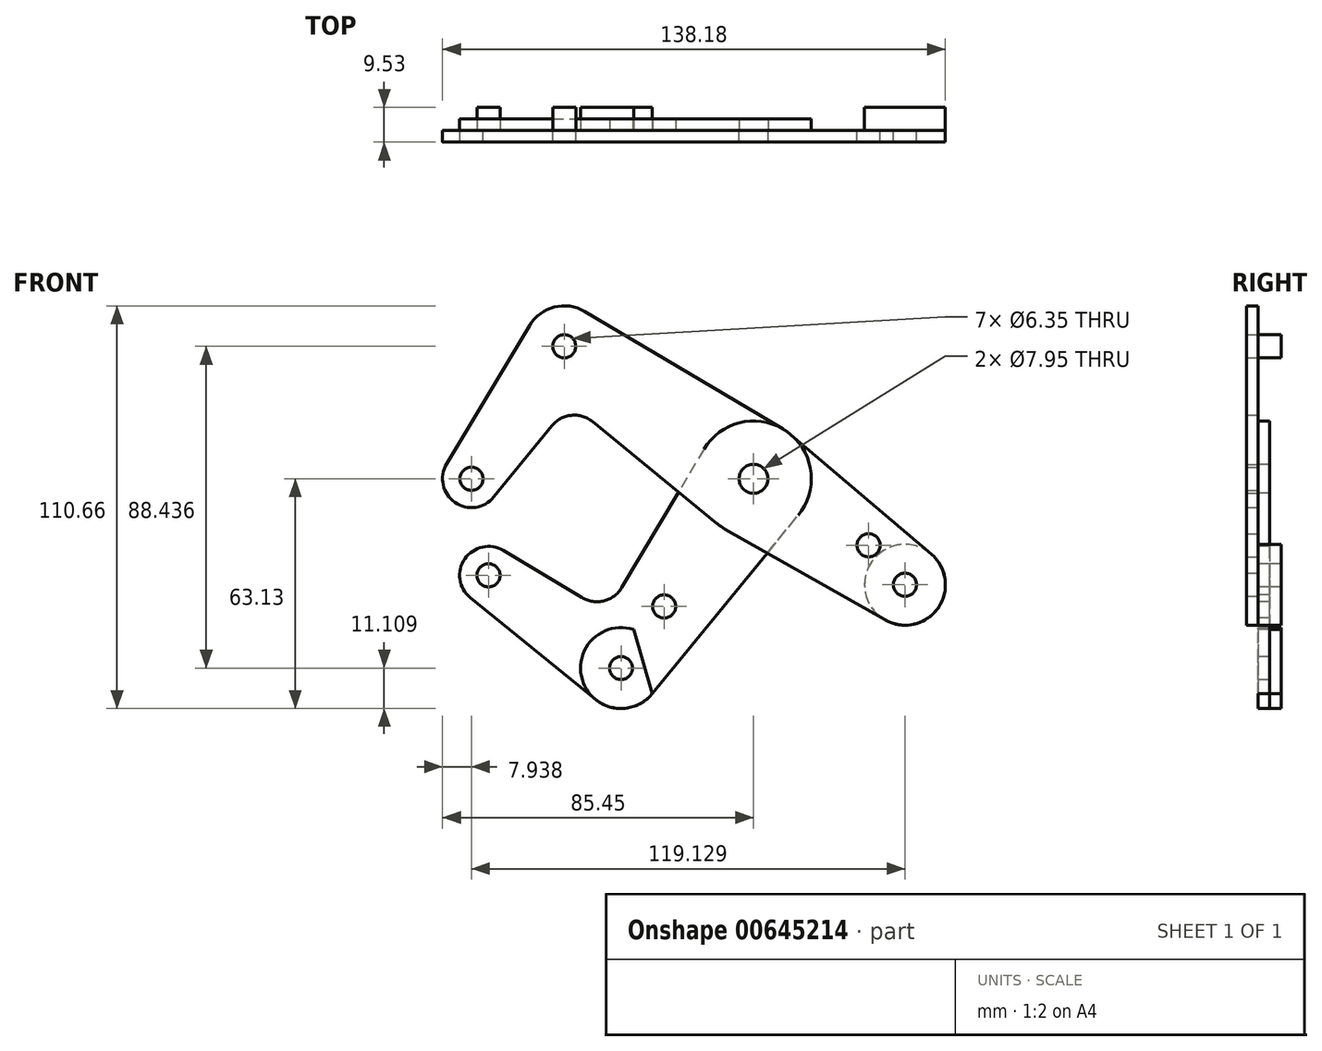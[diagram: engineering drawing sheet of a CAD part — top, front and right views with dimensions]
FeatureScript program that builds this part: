
annotation { "Feature Type Name" : "Feature", "Feature Type Description" : "" }
export const myFeature = defineFeature(function(context is Context, id is Id, definition is map)
    precondition{}
    {
        {
            var Q0;
            Q0=qCreatedBy(makeId("Front.planeOp"),FACE);
            var sketch = newSketch(context, id + "F0", { "sketchPlane" : qUnion([Q0])});
            skLineSegment(sketch, "E0", {"start": v(-77.51, 0) * mm, "end": v(-52.02, 36.41) * mm, "construction": true});
            skCircle(sketch, "E1", {"center": v(-77.51, 0) * mm, "radius": 3.18 * mm});
            skCircle(sketch, "E2", {"center": v(-77.51, 0) * mm, "radius": 7.94 * mm});
            skCircle(sketch, "E3", {"center": v(-52.02, 36.41) * mm, "radius": 3.18 * mm});
            skCircle(sketch, "E4", {"center": v(-52.02, 36.41) * mm, "radius": 11.11 * mm});
            skCircle(sketch, "E5", {"center": v(0, 0) * mm, "radius": 3.18 * mm});
            skCircle(sketch, "E6", {"center": v(0, 0) * mm, "radius": 3.98 * mm});
            skCircle(sketch, "E7", {"center": v(0, 0) * mm, "radius": 15.88 * mm});
            skCircle(sketch, "E8", {"center": v(41.62, -29.13) * mm, "radius": 3.18 * mm});
            skCircle(sketch, "E9", {"center": v(41.62, -29.13) * mm, "radius": 11.11 * mm});
            skCircle(sketch, "E10", {"center": v(31.63, -18.27) * mm, "radius": 3.18 * mm});
            skLineSegment(sketch, "E11", {"start": v(-84.32, 4.08) * mm, "end": v(-61.56, 42.12) * mm});
            skLineSegment(sketch, "E12", {"start": v(-46.35, 45.97) * mm, "end": v(8.1, 13.65) * mm});
            skLineSegment(sketch, "E13", {"start": v(10.28, 12.1) * mm, "end": v(48.81, -20.67) * mm});
            skLineSegment(sketch, "E14", {"start": v(-71.35, -5) * mm, "end": v(-55.46, 14.56) * mm});
            skLineSegment(sketch, "E15", {"start": v(-10.05, -12.29) * mm, "end": v(-44.25, 15.7) * mm});
            skLineSegment(sketch, "E16", {"start": v(-7.84, -13.8) * mm, "end": v(36.13, -38.8) * mm});
            skLineSegment(sketch, "E17", {"start": v(-52.02, 36.41) * mm, "end": v(0, 0) * mm, "construction": true});
            skLineSegment(sketch, "E18", {"start": v(0, 0) * mm, "end": v(41.62, -29.13) * mm, "construction": true});
            skArc(sketch, "E19.filletArc", {"start": v(-44.25, 15.7) * mm, "mid": v(-50.1, 17.46) * mm, "end": v(-55.46, 14.56) * mm});
            skLineSegment(sketch, "E20", {"start": v(0, 0) * mm, "end": v(-36.41, -52.02) * mm, "construction": true});
            skLineSegment(sketch, "E21", {"start": v(-36.41, -52.02) * mm, "end": v(-72.83, -26.53) * mm, "construction": true});
            skCircle(sketch, "E22", {"center": v(-72.83, -26.53) * mm, "radius": 3.18 * mm});
            skCircle(sketch, "E23", {"center": v(-72.83, -26.53) * mm, "radius": 7.94 * mm});
            skCircle(sketch, "E24", {"center": v(-36.41, -52.02) * mm, "radius": 3.18 * mm});
            skCircle(sketch, "E25", {"center": v(-36.41, -52.02) * mm, "radius": 11.11 * mm});
            skCircle(sketch, "E26", {"center": v(-24.57, -35.1) * mm, "radius": 3.18 * mm});
            skLineSegment(sketch, "E27", {"start": v(-77.83, -32.7) * mm, "end": v(-43.42, -60.65) * mm});
            skLineSegment(sketch, "E28", {"start": v(-27.81, -59.06) * mm, "end": v(12.29, -10.05) * mm});
            skLineSegment(sketch, "E29", {"start": v(-68.75, -19.72) * mm, "end": v(-47.13, -32.66) * mm});
            skLineSegment(sketch, "E30", {"start": v(-13.65, 8.1) * mm, "end": v(-36.2, -29.9) * mm});
            skArc(sketch, "E31.filletArc", {"start": v(-47.13, -32.66) * mm, "mid": v(-41.1, -33.55) * mm, "end": v(-36.2, -29.9) * mm});
            skLineSegment(sketch, "E32", {"start": v(-72.83, -26.53) * mm, "end": v(-77.51, 0) * mm, "construction": true});
            skLineSegment(sketch, "E33", {"start": v(-36.41, -52.02) * mm, "end": v(41.62, -29.13) * mm, "construction": true});
            skLineSegment(sketch, "E34", {"start": v(-27.81, -59.06) * mm, "end": v(-32.98, -41.45) * mm});
            skSolve(sketch);
        }
        {
            var Q0;
            Q0=makeQuery(id+"F0.imprint","IMPRINT",FACE,{"disambiguationData":[TD([[makeQuery(id+"F0.imprint","IMPRINT",EDGE,{"derivedFrom":sQuery(id+"F0.wireOp",EDGE,"E3")}),-1.0]])]});
            var Q1;
            {var subQ0=sQuery(id+"F0.wireOp",EDGE,"E11");Q1=makeQuery(id+"F0.imprint","IMPRINT",FACE,{"disambiguationData":[TD([[makeQuery(id+"F0.imprint","IMPRINT",EDGE,{"derivedFrom":subQ0}),-1.0]])]});}
            var Q2;
            Q2=makeQuery(id+"F0.imprint","IMPRINT",FACE,{"disambiguationData":[TD([[makeQuery(id+"F0.imprint","IMPRINT",EDGE,{"derivedFrom":sQuery(id+"F0.wireOp",EDGE,"E1")}),-1.0]])]});
            var Q3;
            Q3=makeQuery(id+"F0.imprint","IMPRINT",FACE,{"disambiguationData":[TD([[makeQuery(id+"F0.imprint","IMPRINT",EDGE,{"derivedFrom":sQuery(id+"F0.wireOp",EDGE,"E6")}),-1.0]])]});
            var Q4;
            {var subQ0=sQuery(id+"F0.wireOp",EDGE,"E15");var subQ1=sQuery(id+"F0.wireOp",EDGE,"E7");var subQ2=makeQuery(id+"F0.imprint","INTERSECT",VERTEX,{"derivedFrom":[subQ1,subQ0]});Q4=makeQuery(id+"F0.imprint","IMPRINT",FACE,{"disambiguationData":[TD([[makeQuery(id+"F0.imprint","IMPRINT",EDGE,{"disambiguationData":[TD([[subQ2,1.0]])],"derivedFrom":subQ1}),-1.0]])]});}
            var Q5;
            {var subQ0=sQuery(id+"F0.wireOp",EDGE,"E16");var subQ1=sQuery(id+"F0.wireOp",EDGE,"E7");var subQ2=makeQuery(id+"F0.imprint","INTERSECT",VERTEX,{"derivedFrom":[subQ1,subQ0]});Q5=makeQuery(id+"F0.imprint","IMPRINT",FACE,{"disambiguationData":[TD([[makeQuery(id+"F0.imprint","IMPRINT",EDGE,{"disambiguationData":[TD([[subQ2,-1.0]])],"derivedFrom":subQ1}),-1.0]])]});}
            var Q6;
            Q6=makeQuery(id+"F0.imprint","IMPRINT",FACE,{"disambiguationData":[TD([[makeQuery(id+"F0.imprint","IMPRINT",EDGE,{"derivedFrom":sQuery(id+"F0.wireOp",EDGE,"E10")}),-1.0]])]});
            var Q7;
            Q7=makeQuery(id+"F0.imprint","IMPRINT",FACE,{"disambiguationData":[TD([[makeQuery(id+"F0.imprint","IMPRINT",EDGE,{"derivedFrom":sQuery(id+"F0.wireOp",EDGE,"E8")}),-1.0]])]});
            extrude(context, id + "F1", {"entities" : qUnion([Q0, Q1, Q2, Q3, Q4, Q5, Q6, Q7]), "depth" : 3.17 * mm, "offsetDistance" : 25.4 * mm});
        }
        {
            var Q0;
            Q0=makeQuery(id+"F0.imprint","IMPRINT",FACE,{"disambiguationData":[TD([[makeQuery(id+"F0.imprint","IMPRINT",EDGE,{"derivedFrom":sQuery(id+"F0.wireOp",EDGE,"E26")}),-1.0]])]});
            var Q1;
            Q1=makeQuery(id+"F0.imprint","IMPRINT",FACE,{"disambiguationData":[TD([[makeQuery(id+"F0.imprint","IMPRINT",EDGE,{"derivedFrom":sQuery(id+"F0.wireOp",EDGE,"E24")}),-1.0]])]});
            var Q2;
            Q2=makeQuery(id+"F0.imprint","IMPRINT",FACE,{"disambiguationData":[TD([[makeQuery(id+"F0.imprint","IMPRINT",EDGE,{"derivedFrom":sQuery(id+"F0.wireOp",EDGE,"E22")}),-1.0]])]});
            var Q3;
            Q3=makeQuery(id+"F0.imprint","IMPRINT",FACE,{"disambiguationData":[TD([[makeQuery(id+"F0.imprint","IMPRINT",EDGE,{"derivedFrom":sQuery(id+"F0.wireOp",EDGE,"E6")}),-1.0]])]});
            var Q4;
            {var subQ0=sQuery(id+"F0.wireOp",EDGE,"E16");var subQ1=sQuery(id+"F0.wireOp",EDGE,"E7");var subQ2=makeQuery(id+"F0.imprint","INTERSECT",VERTEX,{"derivedFrom":[subQ1,subQ0]});Q4=makeQuery(id+"F0.imprint","IMPRINT",FACE,{"disambiguationData":[TD([[makeQuery(id+"F0.imprint","IMPRINT",EDGE,{"disambiguationData":[TD([[subQ2,-1.0]])],"derivedFrom":subQ1}),-1.0]])]});}
            var Q5;
            {var subQ0=sQuery(id+"F0.wireOp",EDGE,"E15");var subQ1=sQuery(id+"F0.wireOp",EDGE,"E7");var subQ2=makeQuery(id+"F0.imprint","INTERSECT",VERTEX,{"derivedFrom":[subQ1,subQ0]});Q5=makeQuery(id+"F0.imprint","IMPRINT",FACE,{"disambiguationData":[TD([[makeQuery(id+"F0.imprint","IMPRINT",EDGE,{"disambiguationData":[TD([[subQ2,1.0]])],"derivedFrom":subQ1}),-1.0]])]});}
            var Q6;
            {var subQ0=sQuery(id+"F0.wireOp",EDGE,"E34");Q6=makeQuery(id+"F0.imprint","IMPRINT",FACE,{"disambiguationData":[TD([[makeQuery(id+"F0.imprint","IMPRINT",EDGE,{"derivedFrom":subQ0}),-1.0]])]});}
            extrude(context, id + "F2", {"entities" : qUnion([Q0, Q1, Q2, Q3, Q4, Q5, Q6]), "oppositeDirection" : true, "depth" : 3.17 * mm, "offsetDistance" : 25.4 * mm});
        }
        {
            var Q0;
            Q0=makeQuery(id+"F0.imprint","IMPRINT",FACE,{"disambiguationData":[TD([[makeQuery(id+"F0.imprint","IMPRINT",EDGE,{"derivedFrom":sQuery(id+"F0.wireOp",EDGE,"E24")}),-1.0]])]});
            var Q1;
            Q1=makeQuery(id+"F0.imprint","IMPRINT",FACE,{"disambiguationData":[TD([[makeQuery(id+"F0.imprint","IMPRINT",EDGE,{"derivedFrom":sQuery(id+"F0.wireOp",EDGE,"E24")}),1.0]])]});
            var Q2;
            Q2=makeQuery(id+"F0.imprint","IMPRINT",FACE,{"disambiguationData":[TD([[makeQuery(id+"F0.imprint","IMPRINT",EDGE,{"derivedFrom":sQuery(id+"F0.wireOp",EDGE,"E22")}),1.0]])]});
            var Q3;
            Q3=makeQuery(id+"F0.imprint","IMPRINT",FACE,{"disambiguationData":[TD([[makeQuery(id+"F0.imprint","IMPRINT",EDGE,{"derivedFrom":sQuery(id+"F0.wireOp",EDGE,"E8")}),-1.0]])]});
            var Q4;
            Q4=makeQuery(id+"F0.imprint","IMPRINT",FACE,{"disambiguationData":[TD([[makeQuery(id+"F0.imprint","IMPRINT",EDGE,{"derivedFrom":sQuery(id+"F0.wireOp",EDGE,"E8")}),1.0]])]});
            var Q5;
            Q5=makeQuery(id+"F0.imprint","IMPRINT",FACE,{"disambiguationData":[TD([[makeQuery(id+"F0.imprint","IMPRINT",EDGE,{"derivedFrom":sQuery(id+"F0.wireOp",EDGE,"E3")}),1.0]])]});
            extrude(context, id + "F3", {"entities" : qUnion([Q0, Q1, Q2, Q3, Q4, Q5]), "oppositeDirection" : true, "depth" : 6.35 * mm, "offsetDistance" : 25.4 * mm});
        }
    });
